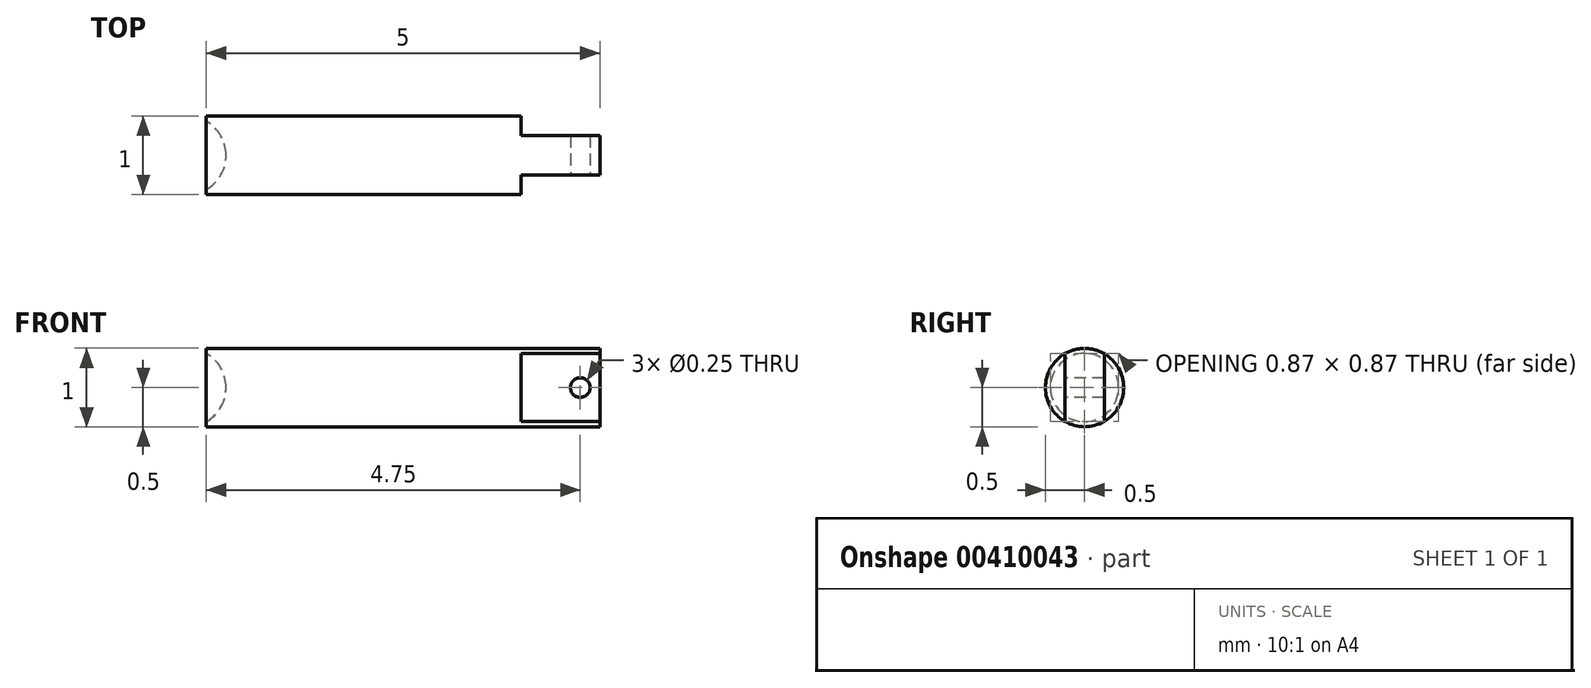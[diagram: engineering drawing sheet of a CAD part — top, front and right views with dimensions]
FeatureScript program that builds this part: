
annotation { "Feature Type Name" : "Feature", "Feature Type Description" : "" }
export const myFeature = defineFeature(function(context is Context, id is Id, definition is map)
    precondition{}
    {
        {
            var Q0;
            Q0=qCreatedBy(makeId("Front.planeOp"),FACE);
            var sketch = newSketch(context, id + "F0", { "sketchPlane" : qUnion([Q0])});
            skLineSegment(sketch, "E0.bottom", {"start": v(0, 0) * mm, "end": v(5, 0) * mm});
            skLineSegment(sketch, "E0.top", {"start": v(0, 0.5) * mm, "end": v(5, 0.5) * mm});
            skLineSegment(sketch, "E0.left", {"start": v(0, 0) * mm, "end": v(0, 0.5) * mm});
            skLineSegment(sketch, "E0.right", {"start": v(5, 0) * mm, "end": v(5, 0.5) * mm});
            skSolve(sketch);
        }
        {
            var Q0;
            Q0=makeQuery(id+"F0.imprint","IMPRINT",FACE,{"disambiguationData":[TD([[makeQuery(id+"F0.imprint","IMPRINT",EDGE,{"derivedFrom":sQuery(id+"F0.wireOp",EDGE,"E0.bottom")}),1.0]])]});
            var Q1;
            Q1=sQuery(id+"F0.wireOp",EDGE,"E0.bottom");
            revolve(context, id + "F1", {"entities" : qUnion([Q0]), "axis" : qUnion([Q1]), "revolveType" : RevolveType.FULL});
        }
        {
            var Q0;
            Q0=qCreatedBy(makeId("Front.planeOp"),FACE);
            var sketch = newSketch(context, id + "F2", { "sketchPlane" : qUnion([Q0])});
            skArc(sketch, "E1", {"start": v(0.25, 0) * mm, "mid": v(-0.25, 0.5) * mm, "end": v(-0.75, 0) * mm});
            skLineSegment(sketch, "E2", {"start": v(0, 0) * mm, "end": v(-0.75, 0) * mm});
            skLineSegment(sketch, "E3", {"start": v(-0.75, 0) * mm, "end": v(0.25, 0) * mm});
            skSolve(sketch);
        }
        {
            var Q0;
            {var subQ0=sQuery(id+"F2.wireOp",EDGE,"E1");Q0=makeQuery(id+"F2.imprint","IMPRINT",FACE,{"disambiguationData":[TD([[makeQuery(id+"F2.imprint","IMPRINT",EDGE,{"derivedFrom":subQ0}),1.0]])]});}
            var Q1;
            Q1=sQuery(id+"F2.wireOp",EDGE,"E3");
            revolve(context, id + "F3", {"operationType" : NewBodyOperationType.REMOVE, "entities" : qUnion([Q0]), "axis" : qUnion([Q1]), "revolveType" : RevolveType.FULL, "oppositeDirection" : true});
        }
        {
            var Q0;
            Q0=makeQuery(id+"F1.opRevolve","SWEPT_FACE",FACE,{"disambiguationData":[OSD([sQuery(id+"F0.wireOp",EDGE,"E0.right")])]});
            var sketch = newSketch(context, id + "F4", { "sketchPlane" : qUnion([Q0])});
            skLineSegment(sketch, "E4.bottom", {"start": v(0.25, 0.75) * mm, "end": v(1.14, 0.75) * mm});
            skLineSegment(sketch, "E4.top", {"start": v(0.25, -1.05) * mm, "end": v(1.14, -1.05) * mm});
            skLineSegment(sketch, "E4.left", {"start": v(0.25, 0.75) * mm, "end": v(0.25, -1.05) * mm});
            skLineSegment(sketch, "E4.right", {"start": v(1.14, 0.75) * mm, "end": v(1.14, -1.05) * mm});
            skLineSegment(sketch, "E5.bottom", {"start": v(-1.08, 1) * mm, "end": v(-0.25, 1) * mm});
            skLineSegment(sketch, "E5.top", {"start": v(-1.08, -1.44) * mm, "end": v(-0.25, -1.44) * mm});
            skLineSegment(sketch, "E5.left", {"start": v(-1.08, 1) * mm, "end": v(-1.08, -1.44) * mm});
            skLineSegment(sketch, "E5.right", {"start": v(-0.25, 1) * mm, "end": v(-0.25, -1.44) * mm});
            skSolve(sketch);
        }
        {
            var Q0;
            {var subQ1=sQuery(id+"F4.wireOp",EDGE,"E5.bottom");Q0=makeQuery(id+"F4.imprint","IMPRINT",FACE,{"disambiguationData":[TD([[makeQuery(id+"F4.imprint","IMPRINT",EDGE,{"derivedFrom":subQ1}),-1.0]])]});}
            var Q1;
            {var subQ4=sQuery(id+"F4.wireOp",EDGE,"E4.bottom");Q1=makeQuery(id+"F4.imprint","IMPRINT",FACE,{"disambiguationData":[TD([[makeQuery(id+"F4.imprint","IMPRINT",EDGE,{"derivedFrom":subQ4}),-1.0]])]});}
            var Q2;
            {var subQ0=sQuery(id+"F4.wireOp",EDGE,"E4.left");var subQ1=makeQuery(id+"F1.opRevolve","SWEPT_EDGE",EDGE,{"disambiguationData":[OSD([sQuery(id+"F0.wireOp",EDGE,"E0.top"),sQuery(id+"F0.wireOp",EDGE,"E0.right")])]});var subQ2=makeQuery(id+"F4.imprint","INTERSECT",VERTEX,{"disambiguationData":[OD(0.0)],"derivedFrom":[subQ1,subQ0]});Q2=makeQuery(id+"F4.imprint","IMPRINT",FACE,{"disambiguationData":[TD([[makeQuery(id+"F4.imprint","IMPRINT",EDGE,{"disambiguationData":[TD([[subQ2,-1.0]])],"derivedFrom":subQ0}),1.0]])]});}
            var Q3;
            {var subQ0=sQuery(id+"F4.wireOp",EDGE,"E5.right");var subQ1=makeQuery(id+"F1.opRevolve","SWEPT_EDGE",EDGE,{"disambiguationData":[OSD([sQuery(id+"F0.wireOp",EDGE,"E0.top"),sQuery(id+"F0.wireOp",EDGE,"E0.right")])]});var subQ2=makeQuery(id+"F4.imprint","INTERSECT",VERTEX,{"disambiguationData":[OD(0.0)],"derivedFrom":[subQ1,subQ0]});Q3=makeQuery(id+"F4.imprint","IMPRINT",FACE,{"disambiguationData":[TD([[makeQuery(id+"F4.imprint","IMPRINT",EDGE,{"disambiguationData":[TD([[subQ2,-1.0]])],"derivedFrom":subQ0}),-1.0]])]});}
            extrude(context, id + "F5", {"entities" : qUnion([Q0, Q1, Q2, Q3]), "operationType" : NewBodyOperationType.REMOVE, "oppositeDirection" : true, "depth" : 1 * mm});
        }
        {
            var Q0;
            Q0=makeQuery(id+"F5.boolean.opBoolean","COPY",FACE,{"derivedFrom":makeQuery(id+"F5.opExtrude","SWEPT_FACE",FACE,{"disambiguationData":[OSD([sQuery(id+"F4.wireOp",EDGE,"E5.right")])]})});
            var sketch = newSketch(context, id + "F6", { "sketchPlane" : qUnion([Q0])});
            skCircle(sketch, "E6", {"center": v(4.75, 0) * mm, "radius": 0.12 * mm});
            skSolve(sketch);
        }
        {
            var Q0;
            Q0=makeQuery(id+"F6.imprint","IMPRINT",FACE,{"disambiguationData":[TD([[makeQuery(id+"F6.imprint","IMPRINT",EDGE,{"derivedFrom":sQuery(id+"F6.wireOp",EDGE,"E6")}),1.0]])]});
            extrude(context, id + "F7", {"entities" : qUnion([Q0]), "operationType" : NewBodyOperationType.REMOVE, "oppositeDirection" : true, "depth" : 25 * mm});
        }
    });
